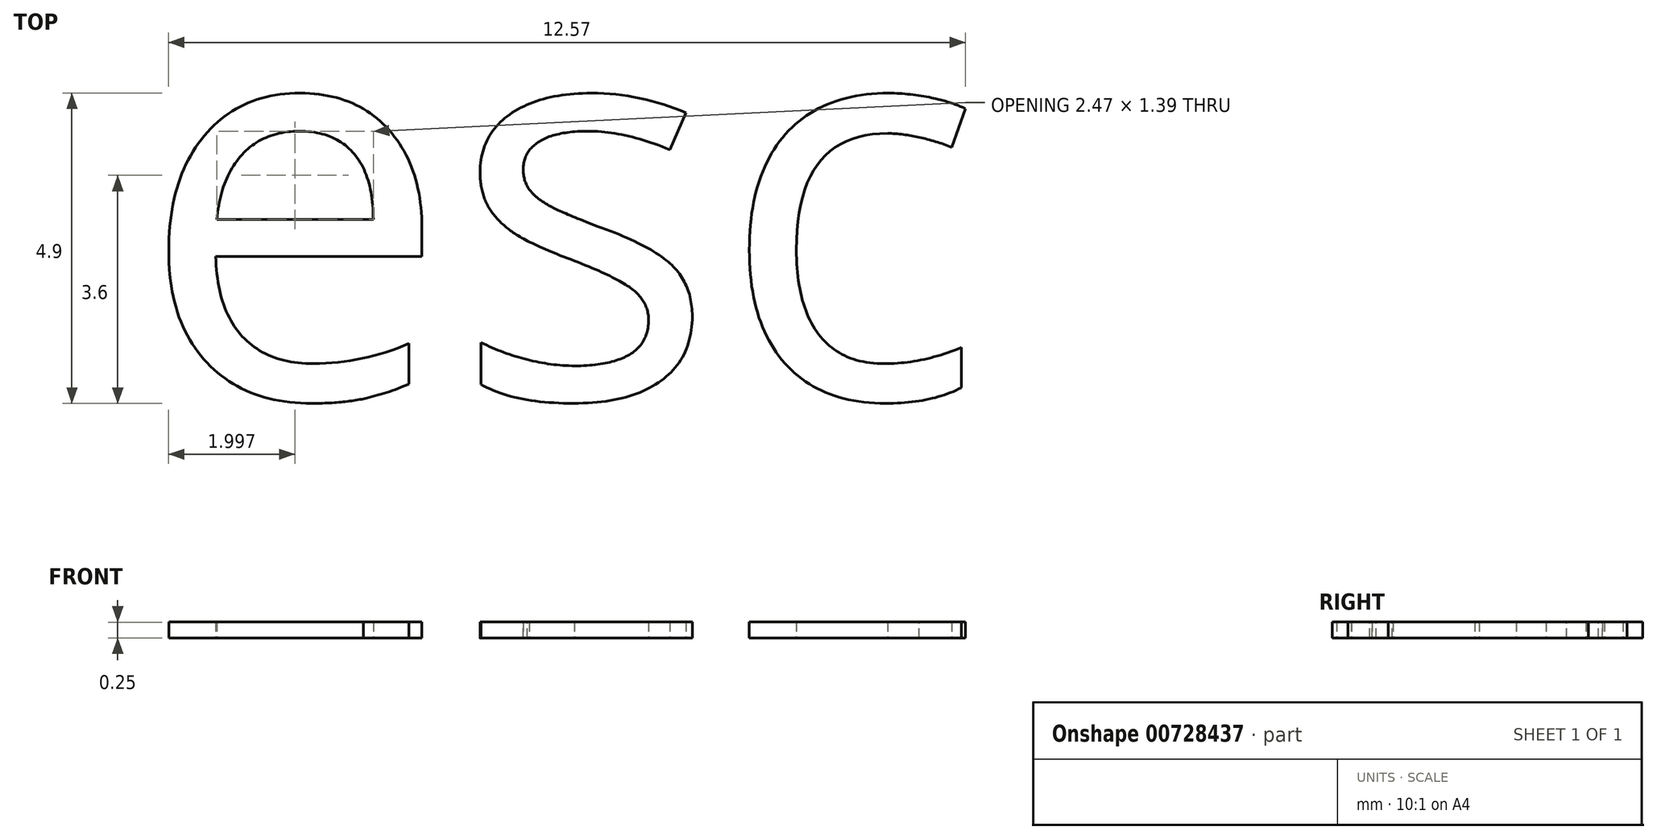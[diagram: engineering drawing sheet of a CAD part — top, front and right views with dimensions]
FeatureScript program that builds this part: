
annotation { "Feature Type Name" : "Feature", "Feature Type Description" : "" }
export const myFeature = defineFeature(function(context is Context, id is Id, definition is map)
    precondition{}
    {
        {
            var Q0;
            Q0=qCreatedBy(makeId("Top.planeOp"),FACE);
            var sketch = newSketch(context, id + "F0", { "sketchPlane" : qUnion([Q0])});
            skText(sketch, "E0", { "text": "esc\n", "fontName": "OpenSans-Regular.ttf"});
            const initialGuessF0  = {"E0": [-0.03407, 0.01259, 1, 0, 0.00635]};
            skSetInitialGuess(sketch, initialGuessF0);
            skSolve(sketch);
        }
        {
            var Q0;
            Q0 = qSketchRegion(id + "F0", true);
            extrude(context, id + "F1", {"entities" : qUnion([Q0]), "depth" : 0.25 * mm, "offsetDistance" : 25.4 * mm});
        }
    });
